# Revit family: DockSeal_BlueGiant_BG200D
name_source: partatom
category: Specialty Equipment
units: mm (PartAtom-declared; Revit-internal decimal feet)

## family parameters
Always vertical = Yes
Cut with Voids When Loaded = No
Enable Cutting in Views = No
Maintain Annotation Orientation = No
Part Type = Normal
Room Calculation Point = No
Round Connector Dimension = Use Diameter
Shared = No
Work Plane-Based = Yes

## types (4) — shared parameters
Assembly Code = E1030300
Construction Details = http://www.arcat.com
Default Elevation = 4' - 0"
Door Opening Height = 10' - 0"
Door Opening Width = 8' - 0"
Fabric Color = Fabric - Blue Giant - 22oz HT Blue Vinyl
Green Building-LEED = http://www.arcat.com
Header Height = 2' - 0"
Installation_Fabricaton = http://www.bluegiant.com
Keynote = 11160
Manufacturer = Blue Giant Equipment Corp.
Manufacturer Fax = 905-457-2313
Manufacturer Website = http://www.bluegiant.com
Model = BG200D
Pad Height = 9' - 0"
Product Data = http://www.arcat.com
Product Properties = http://www.arcat.com
Projection = 0' - 10"
Sales Information = http://www.bluegiant.com
Send Message = http://admin.arcat.com
SpecWizard = http://www.arcat.com
Specification = http://www.arcat.com
Truck Guide Color = Fabric - Blue Giant - Yellow Guide
URL = http://www.bluegiant.com
zero-valued in all types: Expected Lifespan (Years), Maintenance Schedule (Months), Warranty Duration (Years)

## per-type parameters (varying)
| type | Description | pad-width | sidepadoffset | taper-bottom | taper-header-bottom | taper-header-top | taper-top |
| Standard Unit | Blue Giant BG200D Standard Unit Dock Seal | 1' - 0" | 1' - 4" | 0' - 10" | 0' - 10" | 0' - 10" | 0' - 10" |
| Varible Wedge Unit | Blue Giant BG200D Varible Wedge Unit Dock Seal | 0' - 8" | 1' - 0" | 0' - 10" | 0' - 10" | 0' - 10" | 0' - 10" |
| Tapered Unit Incline | Blue Giant BG200D Tapered Unit Incline Dock Seal | 1' - 0" | 1' - 4" | 0' - 10" | 1' - 4" | 1' - 6" | 1' - 4" |
| Tapered Unit Decline | Blue Giant BG200D Tapered Unit Decline Dock Seal | 1' - 0" | 1' - 4" | 1' - 4" | 0' - 11 1/2" | 0' - 10" | 0' - 11" |

type visibility flags: 4 boolean params named "<type name>" — each type sets only its own to Yes (folded from table)

## geometry (parser evidence)
native form markers: Blend x6, Sweep x6
no freeform markers — native parametric forms only
